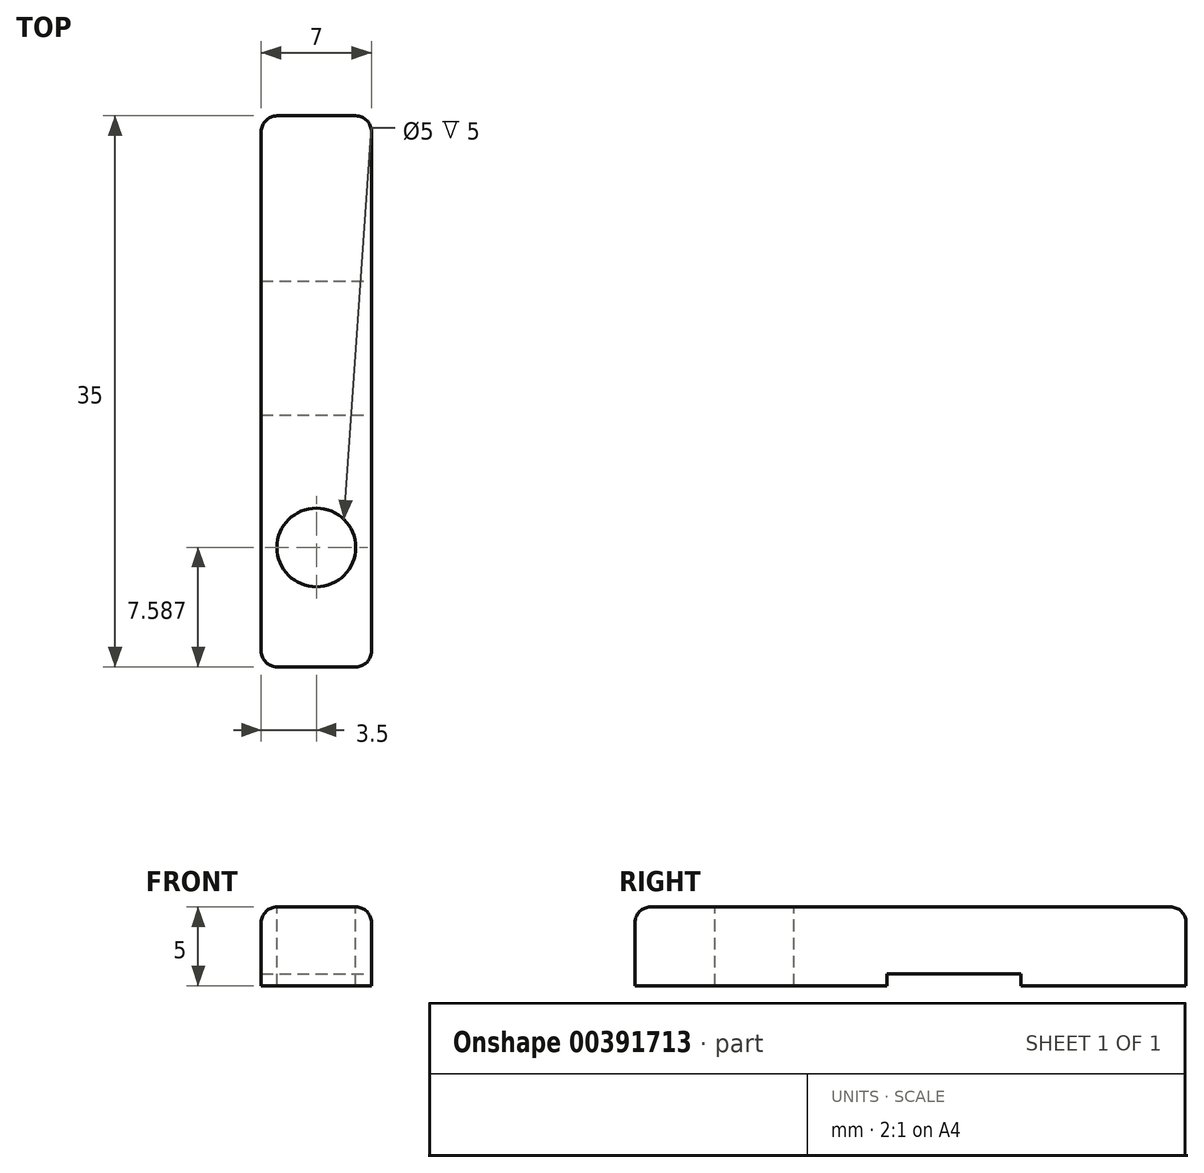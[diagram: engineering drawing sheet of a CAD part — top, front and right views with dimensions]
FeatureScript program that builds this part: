
annotation { "Feature Type Name" : "Feature", "Feature Type Description" : "" }
export const myFeature = defineFeature(function(context is Context, id is Id, definition is map)
    precondition{}
    {
        {
            var Q0;
            Q0=qCreatedBy(makeId("Right.planeOp"),FACE);
            var sketch = newSketch(context, id + "F0", { "sketchPlane" : qUnion([Q0])});
            skLineSegment(sketch, "E0", {"start": v(0, 0) * mm, "end": v(35, 0) * mm});
            skLineSegment(sketch, "E1", {"start": v(35, 0) * mm, "end": v(35, -5) * mm});
            skLineSegment(sketch, "E2", {"start": v(35, -5) * mm, "end": v(24.5, -5) * mm});
            skLineSegment(sketch, "E3", {"start": v(24.5, -5) * mm, "end": v(24.5, -4.25) * mm});
            skLineSegment(sketch, "E4", {"start": v(24.5, -4.25) * mm, "end": v(16, -4.25) * mm});
            skLineSegment(sketch, "E5", {"start": v(16, -4.25) * mm, "end": v(16, -5) * mm});
            skLineSegment(sketch, "E6", {"start": v(16, -5) * mm, "end": v(0, -5) * mm});
            skLineSegment(sketch, "E7", {"start": v(0, -5) * mm, "end": v(0, 0) * mm});
            skSolve(sketch);
        }
        {
            var Q0;
            Q0=makeQuery(id+"F0.imprint","IMPRINT",FACE,{"disambiguationData":[TD([[makeQuery(id+"F0.imprint","IMPRINT",EDGE,{"derivedFrom":sQuery(id+"F0.wireOp",EDGE,"E0")}),-1.0]])]});
            extrude(context, id + "F1", {"entities" : qUnion([Q0]), "oppositeDirection" : true, "depth" : 7 * mm});
        }
        {
            var Q0;
            Q0=makeQuery(id+"F1.opExtrude","SWEPT_FACE",FACE,{"disambiguationData":[OSD([sQuery(id+"F0.wireOp",EDGE,"E0")])]});
            var sketch = newSketch(context, id + "F2", { "sketchPlane" : qUnion([Q0])});
            skCircle(sketch, "E8", {"center": v(-3.5, 7.59) * mm, "radius": 2.5 * mm});
            skLineSegment(sketch, "E9", {"start": v(-3.5, 0) * mm, "end": v(-3.5, 11.84) * mm, "construction": true});
            skSolve(sketch);
        }
        {
            var Q0;
            Q0=makeQuery(id+"F2.imprint","IMPRINT",FACE,{"disambiguationData":[TD([[makeQuery(id+"F2.imprint","IMPRINT",EDGE,{"derivedFrom":sQuery(id+"F2.wireOp",EDGE,"E8")}),1.0]])]});
            var Q1;
            Q1=sQuery(id+"F2.wireOp",EDGE,"E8");
            extrude(context, id + "F3", {"entities" : qUnion([Q0]), "operationType" : NewBodyOperationType.REMOVE, "surfaceEntities" : qUnion([Q1]), "endBound" : BoundingType.THROUGH_ALL, "oppositeDirection" : true, "depth" : 25 * mm});
        }
        {
            var Q0;
            Q0=makeQuery(id+"F1.opExtrude","SWEPT_EDGE",EDGE,{"disambiguationData":[OSD([sQuery(id+"F0.wireOp",EDGE,"E0"),sQuery(id+"F0.wireOp",EDGE,"E1")])]});
            var Q1;
            Q1=makeQuery(id+"F1.opExtrude","CAP_EDGE",EDGE,{"disambiguationData":[OSD([sQuery(id+"F0.wireOp",EDGE,"E0")])],"isStart":false});
            var Q2;
            Q2=makeQuery(id+"F1.opExtrude","SWEPT_EDGE",EDGE,{"disambiguationData":[OSD([sQuery(id+"F0.wireOp",EDGE,"E0"),sQuery(id+"F0.wireOp",EDGE,"E7")])]});
            var Q3;
            Q3=makeQuery(id+"F1.opExtrude","CAP_EDGE",EDGE,{"disambiguationData":[OSD([sQuery(id+"F0.wireOp",EDGE,"E0")])],"isStart":true});
            var Q4;
            Q4=makeQuery(id+"F1.opExtrude","CAP_EDGE",EDGE,{"disambiguationData":[OSD([sQuery(id+"F0.wireOp",EDGE,"E7")])],"isStart":true});
            var Q5;
            Q5=makeQuery(id+"F1.opExtrude","CAP_EDGE",EDGE,{"disambiguationData":[OSD([sQuery(id+"F0.wireOp",EDGE,"E1")])],"isStart":true});
            var Q6;
            Q6=makeQuery(id+"F1.opExtrude","CAP_EDGE",EDGE,{"disambiguationData":[OSD([sQuery(id+"F0.wireOp",EDGE,"E1")])],"isStart":false});
            var Q7;
            Q7=makeQuery(id+"F1.opExtrude","CAP_EDGE",EDGE,{"disambiguationData":[OSD([sQuery(id+"F0.wireOp",EDGE,"E7")])],"isStart":false});
            fillet(context, id + "F4", {"entities" : qUnion([Q0, Q1, Q2, Q3, Q4, Q5, Q6, Q7]), "radius" : 1 * mm, "tangentPropagation" : true, "allowEdgeOverflow" : false});
        }
    });
